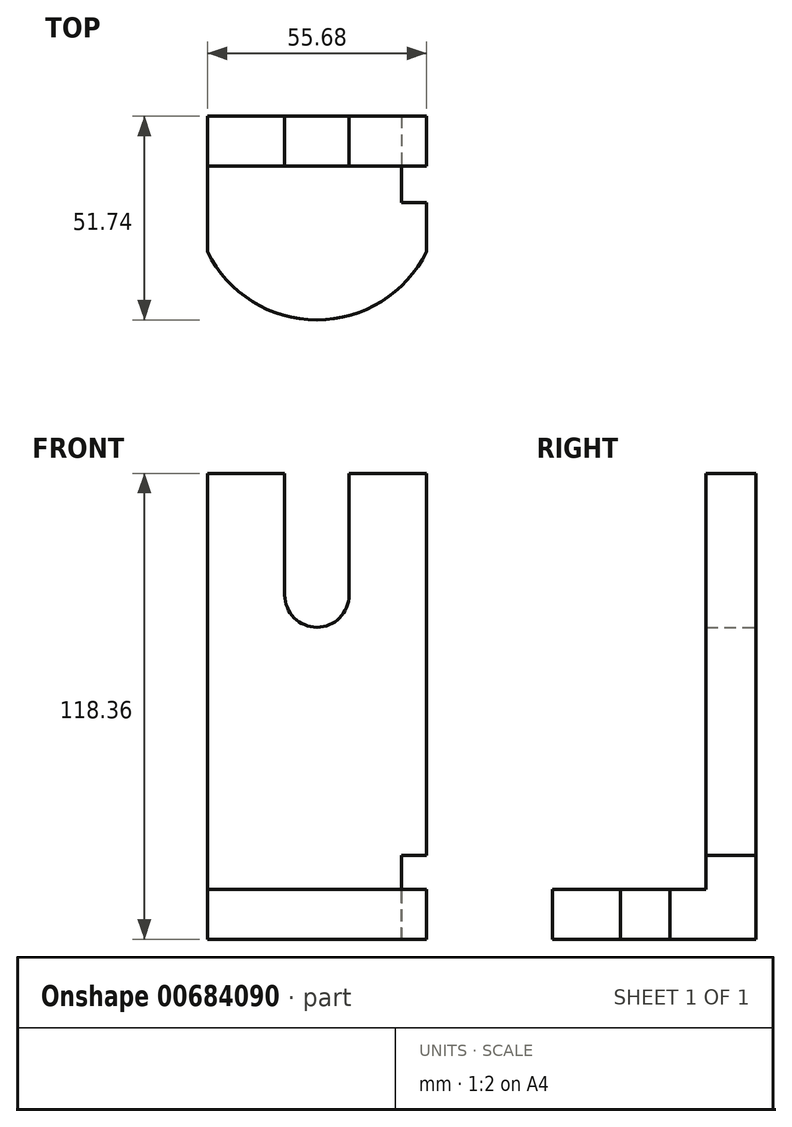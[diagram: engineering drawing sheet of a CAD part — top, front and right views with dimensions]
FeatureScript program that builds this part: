
annotation { "Feature Type Name" : "Feature", "Feature Type Description" : "" }
export const myFeature = defineFeature(function(context is Context, id is Id, definition is map)
    precondition{}
    {
        {
            var Q0;
            Q0=qCreatedBy(makeId("Top.planeOp"),FACE);
            var sketch = newSketch(context, id + "F0", { "sketchPlane" : qUnion([Q0])});
            skLineSegment(sketch, "E0", {"start": v(0, 0) * mm, "end": v(-27.84, 0) * mm});
            skLineSegment(sketch, "E1", {"start": v(-27.84, 0) * mm, "end": v(-27.84, -34.41) * mm});
            skArc(sketch, "E2", {"start": v(-27.84, -34.41) * mm, "mid": v(-16.4, -47.05) * mm, "end": v(0, -51.74) * mm});
            skLineSegment(sketch, "E3.MirrorCS", {"start": v(27.84, 0) * mm, "end": v(27.84, -34.41) * mm});
            skLineSegment(sketch, "E4.MirrorCS", {"start": v(0, 0) * mm, "end": v(27.84, 0) * mm});
            skArc(sketch, "E5.MirrorCS", {"start": v(27.84, -34.41) * mm, "mid": v(16.4, -47.05) * mm, "end": v(0, -51.74) * mm});
            skSolve(sketch);
        }
        {
            var Q0;
            Q0 = qSketchRegion(id + "F0", true);
            extrude(context, id + "F1", {"entities" : qUnion([Q0]), "depth" : 118.36 * mm, "offsetDistance" : 25.4 * mm});
        }
        {
            var Q0;
            Q0=qCreatedBy(makeId("Right.planeOp"),FACE);
            var sketch = newSketch(context, id + "F2", { "sketchPlane" : qUnion([Q0])});
            skLineSegment(sketch, "E6.0", {"start": v(-12.7, 118.36) * mm, "end": v(-12.7, 12.7) * mm});
            skLineSegment(sketch, "E7.0", {"start": v(-12.7, 12.7) * mm, "end": v(-80.96, 12.7) * mm});
            skLineSegment(sketch, "E8", {"start": v(-80.96, 12.7) * mm, "end": v(-80.96, 118.36) * mm});
            skLineSegment(sketch, "E9", {"start": v(-80.96, 118.36) * mm, "end": v(-12.7, 118.36) * mm});
            skSolve(sketch);
        }
        {
            var Q0;
            Q0 = qSketchRegion(id + "F2", true);
            extrude(context, id + "F3", {"entities" : qUnion([Q0]), "operationType" : NewBodyOperationType.REMOVE, "endBound" : BoundingType.THROUGH_ALL, "oppositeDirection" : true, "depth" : 25.4 * mm, "offsetDistance" : 25.4 * mm, "hasSecondDirection" : true, "secondDirectionBound" : SecondDirectionBoundingType.THROUGH_ALL, "secondDirectionOppositeDirection" : false, "secondDirectionDepth" : 25.4 * mm});
        }
        {
            var Q0;
            Q0=makeQuery(id+"F1.opExtrude","SWEPT_FACE",FACE,{"disambiguationData":[OSD([sQuery(id+"F0.wireOp",EDGE,"E3.MirrorCS")])]});
            var sketch = newSketch(context, id + "F4", { "sketchPlane" : qUnion([Q0])});
            skLineSegment(sketch, "E10.bottom", {"start": v(0, 0) * mm, "end": v(-21.92, 0) * mm});
            skLineSegment(sketch, "E10.top", {"start": v(0, 21.34) * mm, "end": v(-21.92, 21.34) * mm});
            skLineSegment(sketch, "E10.left", {"start": v(0, 0) * mm, "end": v(0, 21.34) * mm});
            skLineSegment(sketch, "E10.right", {"start": v(-21.92, 0) * mm, "end": v(-21.92, 21.34) * mm});
            skSolve(sketch);
        }
        {
            var Q0;
            {var subQ0=sQuery(id+"F4.wireOp",EDGE,"E10.right");var subQ1=sQuery(id+"F4.wireOp",EDGE,"E10.top");var subQ2=makeQuery(id+"F4.imprint","INTERSECT",VERTEX,{"derivedFrom":[subQ1,subQ0]});Q0=makeQuery(id+"F4.imprint","IMPRINT",FACE,{"disambiguationData":[TD([[makeQuery(id+"F4.imprint","IMPRINT",EDGE,{"disambiguationData":[TD([[subQ2,1.0]])],"derivedFrom":subQ1}),1.0]])]});}
            var Q1;
            {var subQ1=sQuery(id+"F4.wireOp",EDGE,"E10.bottom");Q1=makeQuery(id+"F4.imprint","IMPRINT",FACE,{"disambiguationData":[TD([[makeQuery(id+"F4.imprint","IMPRINT",EDGE,{"derivedFrom":subQ1}),-1.0]])]});}
            extrude(context, id + "F5", {"entities" : qUnion([Q0, Q1]), "operationType" : NewBodyOperationType.REMOVE, "oppositeDirection" : true, "depth" : 6.35 * mm, "offsetDistance" : 25.4 * mm});
        }
        {
            var Q0;
            Q0=makeQuery(id+"F1.opExtrude","SWEPT_FACE",FACE,{"disambiguationData":[OSD([sQuery(id+"F0.wireOp",EDGE,"E0"),sQuery(id+"F0.wireOp",EDGE,"E4.MirrorCS")])]});
            var sketch = newSketch(context, id + "F6", { "sketchPlane" : qUnion([Q0])});
            skLineSegment(sketch, "E11", {"start": v(0, 0) * mm, "end": v(0, 139.81) * mm, "construction": true});
            skLineSegment(sketch, "E12", {"start": v(0, 118.36) * mm, "end": v(-8.17, 118.36) * mm});
            skLineSegment(sketch, "E13", {"start": v(-8.17, 118.36) * mm, "end": v(-8.17, 87.45) * mm});
            skArc(sketch, "E14", {"start": v(-8.17, 87.45) * mm, "mid": v(-5.78, 81.67) * mm, "end": v(0, 79.28) * mm});
            skLineSegment(sketch, "E15.MirrorCS", {"start": v(8.17, 118.36) * mm, "end": v(8.17, 87.45) * mm});
            skLineSegment(sketch, "E16.MirrorCS", {"start": v(0, 118.36) * mm, "end": v(8.17, 118.36) * mm});
            skArc(sketch, "E17.MirrorCS", {"start": v(8.17, 87.45) * mm, "mid": v(5.78, 81.67) * mm, "end": v(0, 79.28) * mm});
            skSolve(sketch);
        }
        {
            var Q0;
            Q0 = qSketchRegion(id + "F6", true);
            extrude(context, id + "F7", {"entities" : qUnion([Q0]), "operationType" : NewBodyOperationType.REMOVE, "endBound" : BoundingType.THROUGH_ALL, "oppositeDirection" : true, "depth" : 25.4 * mm, "offsetDistance" : 25.4 * mm});
        }
    });
